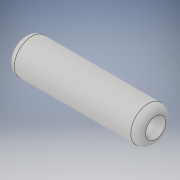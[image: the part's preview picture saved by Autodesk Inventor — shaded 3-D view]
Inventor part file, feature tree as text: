
AUTODESK INVENTOR PART (.ipt)
format: ipt  version: 2018 (Build 220112000, 112)  size: 134,144 bytes
history: native  units: in
note: dims shown in document units (in); Inventor stores cm internally (conversion verified against a paired STEP export)
features: other x2, revolve x1, fillet x1, sketch x1
ambient origin geometry x8: Origin, YZ Plane, XZ Plane, XY Plane, X Axis, Y Axis, Z Axis, Center Point
bodies: Body1 (feature_tree)
feature tree (5):
  other  "Annotations"
  revolve  "Revolution1"  [1 undecoded]
  fillet  "Fillet3"  Radius=0.156in
  sketch  "Sketch2"  dims[d17=4.469in d18=0.25in d19=0.156in d20=0.25in d24=0.25in d25=0.25in d26=4.469in d27=0.0938in d28=90.0deg d29=0.25in d21=0.5567in]
  other  "Linear Dimension 1"
note: 1 required parameter value undecoded (feature->parameter linkage not recoverable at this tier; creation-order binding heuristic only, values carry confidence <= 0.55)
